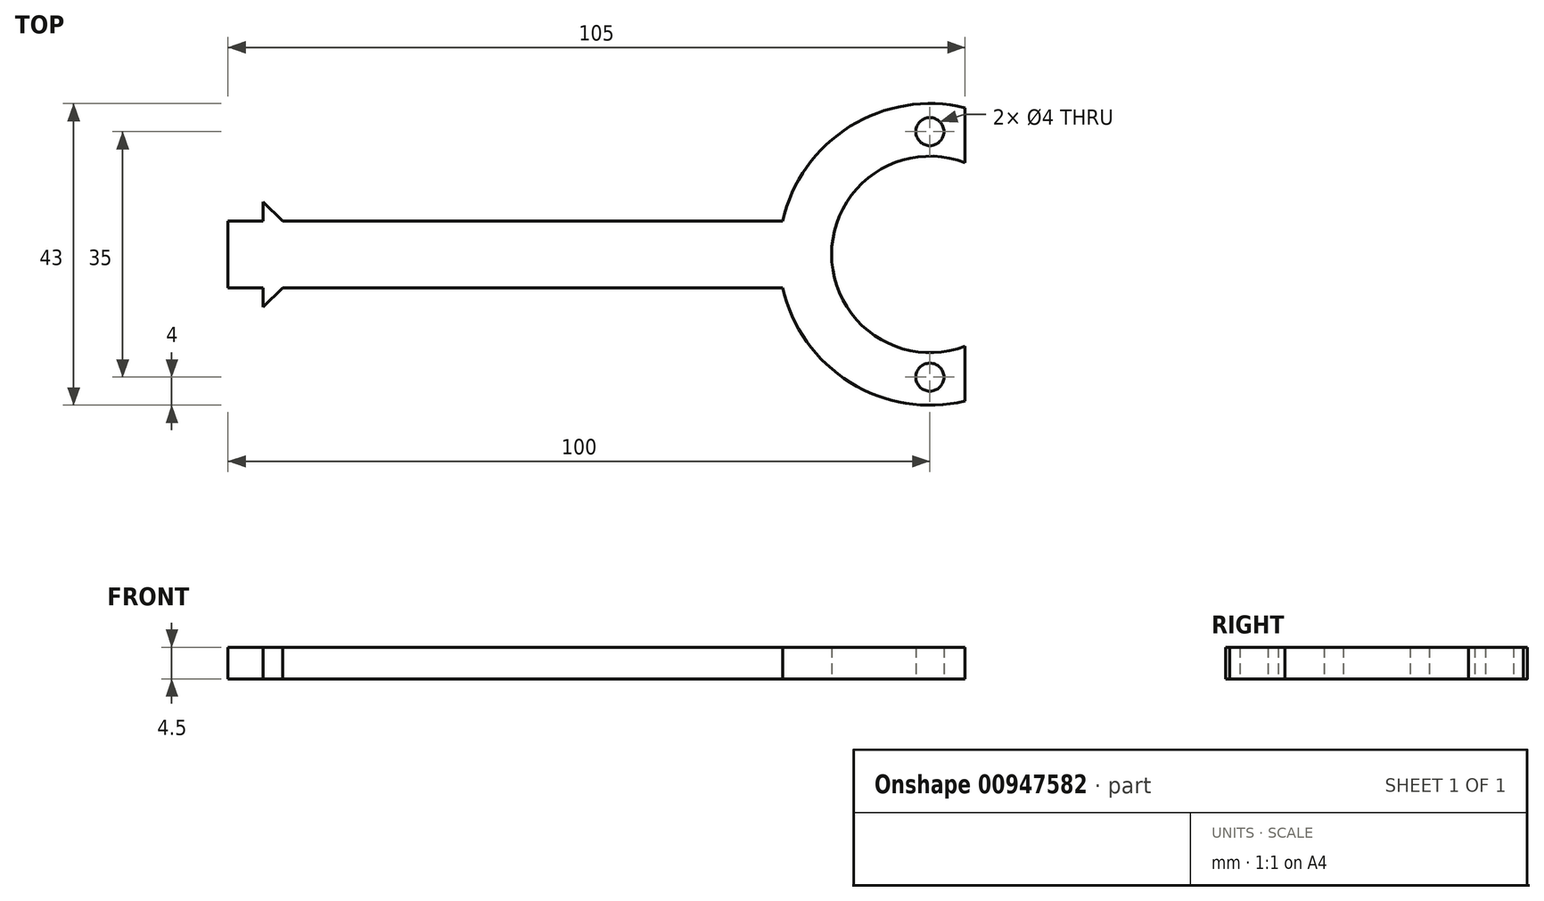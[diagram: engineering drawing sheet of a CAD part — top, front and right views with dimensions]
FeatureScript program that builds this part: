
annotation { "Feature Type Name" : "Feature", "Feature Type Description" : "" }
export const myFeature = defineFeature(function(context is Context, id is Id, definition is map)
    precondition{}
    {
        {
            var Q0;
            Q0=qCreatedBy(makeId("Top.planeOp"),FACE);
            var sketch = newSketch(context, id + "F0", { "sketchPlane" : qUnion([Q0])});
            skLineSegment(sketch, "E0.bottom", {"start": v(-50, 4.75) * mm, "end": v(50, 4.75) * mm});
            skLineSegment(sketch, "E0.top", {"start": v(-50, -4.75) * mm, "end": v(50, -4.75) * mm});
            skLineSegment(sketch, "E0.left", {"start": v(-50, 4.75) * mm, "end": v(-50, -4.75) * mm});
            skLineSegment(sketch, "E0.right", {"start": v(50, 4.75) * mm, "end": v(50, -4.75) * mm});
            skCircle(sketch, "E1", {"center": v(50, 0) * mm, "radius": 14 * mm});
            skCircle(sketch, "E2", {"center": v(50, 0) * mm, "radius": 21.5 * mm});
            skLineSegment(sketch, "E3", {"start": v(50, 39.25) * mm, "end": v(50, -32.9) * mm});
            skCircle(sketch, "E4", {"center": v(50, 17.5) * mm, "radius": 2 * mm});
            skCircle(sketch, "E5", {"center": v(50, -17.5) * mm, "radius": 2 * mm});
            skLineSegment(sketch, "E6", {"start": v(55, 39.07) * mm, "end": v(55, -32.83) * mm});
            skLineSegment(sketch, "E7", {"start": v(-45, 7.5) * mm, "end": v(-45, -7.5) * mm});
            skLineSegment(sketch, "E8", {"start": v(-45, -7.5) * mm, "end": v(-37.5, 0) * mm});
            skLineSegment(sketch, "E9", {"start": v(-37.5, 0) * mm, "end": v(-45, 7.5) * mm});
            skSolve(sketch);
        }
        {
            var Q0;
            {var subQ0=sQuery(id+"F0.wireOp",EDGE,"E0.left");Q0=makeQuery(id+"F0.imprint","IMPRINT",FACE,{"disambiguationData":[TD([[makeQuery(id+"F0.imprint","IMPRINT",EDGE,{"derivedFrom":subQ0}),1.0]])]});}
            var Q1;
            {var subQ0=sQuery(id+"F0.wireOp",EDGE,"E2");var subQ1=sQuery(id+"F0.wireOp",EDGE,"E0.bottom");var subQ2=makeQuery(id+"F0.imprint","INTERSECT",VERTEX,{"derivedFrom":[subQ1,subQ0]});Q1=makeQuery(id+"F0.imprint","IMPRINT",FACE,{"disambiguationData":[TD([[makeQuery(id+"F0.imprint","IMPRINT",EDGE,{"disambiguationData":[TD([[subQ2,-1.0]])],"derivedFrom":subQ1}),-1.0]])]});}
            var Q2;
            {var subQ1=sQuery(id+"F0.wireOp",EDGE,"E2");var subQ6=sQuery(id+"F0.wireOp",EDGE,"E0.bottom");var subQ9=makeQuery(id+"F0.imprint","INTERSECT",VERTEX,{"derivedFrom":[subQ6,subQ1]});Q2=makeQuery(id+"F0.imprint","IMPRINT",FACE,{"disambiguationData":[TD([[makeQuery(id+"F0.imprint","IMPRINT",EDGE,{"disambiguationData":[TD([[subQ9,-1.0]])],"derivedFrom":subQ6}),1.0]])]});}
            var Q3;
            {var subQ1=sQuery(id+"F0.wireOp",EDGE,"E2");var subQ3=sQuery(id+"F0.wireOp",EDGE,"E0.top");var subQ4=makeQuery(id+"F0.imprint","INTERSECT",VERTEX,{"derivedFrom":[subQ3,subQ1]});Q3=makeQuery(id+"F0.imprint","IMPRINT",FACE,{"disambiguationData":[TD([[makeQuery(id+"F0.imprint","IMPRINT",EDGE,{"disambiguationData":[TD([[subQ4,-1.0]])],"derivedFrom":subQ3}),-1.0]])]});}
            var Q4;
            {var subQ0=sQuery(id+"F0.wireOp",EDGE,"E3");var subQ1=sQuery(id+"F0.wireOp",EDGE,"E1");var subQ2=makeQuery(id+"F0.imprint","INTERSECT",VERTEX,{"disambiguationData":[OD(1.0)],"derivedFrom":[subQ1,subQ0]});Q4=makeQuery(id+"F0.imprint","IMPRINT",FACE,{"disambiguationData":[TD([[makeQuery(id+"F0.imprint","IMPRINT",EDGE,{"disambiguationData":[TD([[subQ2,-1.0]])],"derivedFrom":subQ1}),-1.0]])]});}
            var Q5;
            {var subQ0=sQuery(id+"F0.wireOp",EDGE,"E3");var subQ1=sQuery(id+"F0.wireOp",EDGE,"E1");var subQ2=makeQuery(id+"F0.imprint","INTERSECT",VERTEX,{"disambiguationData":[OD(0.0)],"derivedFrom":[subQ1,subQ0]});Q5=makeQuery(id+"F0.imprint","IMPRINT",FACE,{"disambiguationData":[TD([[makeQuery(id+"F0.imprint","IMPRINT",EDGE,{"disambiguationData":[TD([[subQ2,1.0]])],"derivedFrom":subQ1}),-1.0]])]});}
            var Q6;
            {var subQ0=sQuery(id+"F0.wireOp",EDGE,"E9");var subQ6=sQuery(id+"F0.wireOp",EDGE,"E0.bottom");var subQ9=makeQuery(id+"F0.imprint","INTERSECT",VERTEX,{"derivedFrom":[subQ6,subQ0]});Q6=makeQuery(id+"F0.imprint","IMPRINT",FACE,{"disambiguationData":[TD([[makeQuery(id+"F0.imprint","IMPRINT",EDGE,{"disambiguationData":[TD([[subQ9,-1.0]])],"derivedFrom":subQ6}),-1.0]])]});}
            var Q7;
            {var subQ5=sQuery(id+"F0.wireOp",EDGE,"E7");var subQ6=sQuery(id+"F0.wireOp",EDGE,"E0.bottom");var subQ7=makeQuery(id+"F0.imprint","INTERSECT",VERTEX,{"derivedFrom":[subQ6,subQ5]});Q7=makeQuery(id+"F0.imprint","IMPRINT",FACE,{"disambiguationData":[TD([[makeQuery(id+"F0.imprint","IMPRINT",EDGE,{"disambiguationData":[TD([[subQ7,-1.0]])],"derivedFrom":subQ6}),-1.0]])]});}
            var Q8;
            {var subQ0=sQuery(id+"F0.wireOp",EDGE,"E7");var subQ1=sQuery(id+"F0.wireOp",EDGE,"E0.bottom");var subQ2=makeQuery(id+"F0.imprint","INTERSECT",VERTEX,{"derivedFrom":[subQ1,subQ0]});Q8=makeQuery(id+"F0.imprint","IMPRINT",FACE,{"disambiguationData":[TD([[makeQuery(id+"F0.imprint","IMPRINT",EDGE,{"disambiguationData":[TD([[subQ2,-1.0]])],"derivedFrom":subQ1}),1.0]])]});}
            var Q9;
            {var subQ0=sQuery(id+"F0.wireOp",EDGE,"E7");var subQ1=sQuery(id+"F0.wireOp",EDGE,"E0.top");var subQ2=makeQuery(id+"F0.imprint","INTERSECT",VERTEX,{"derivedFrom":[subQ1,subQ0]});Q9=makeQuery(id+"F0.imprint","IMPRINT",FACE,{"disambiguationData":[TD([[makeQuery(id+"F0.imprint","IMPRINT",EDGE,{"disambiguationData":[TD([[subQ2,-1.0]])],"derivedFrom":subQ1}),-1.0]])]});}
            extrude(context, id + "F1", {"entities" : qUnion([Q0, Q1, Q2, Q3, Q4, Q5, Q6, Q7, Q8, Q9]), "depth" : 4.5 * mm});
        }
    });
